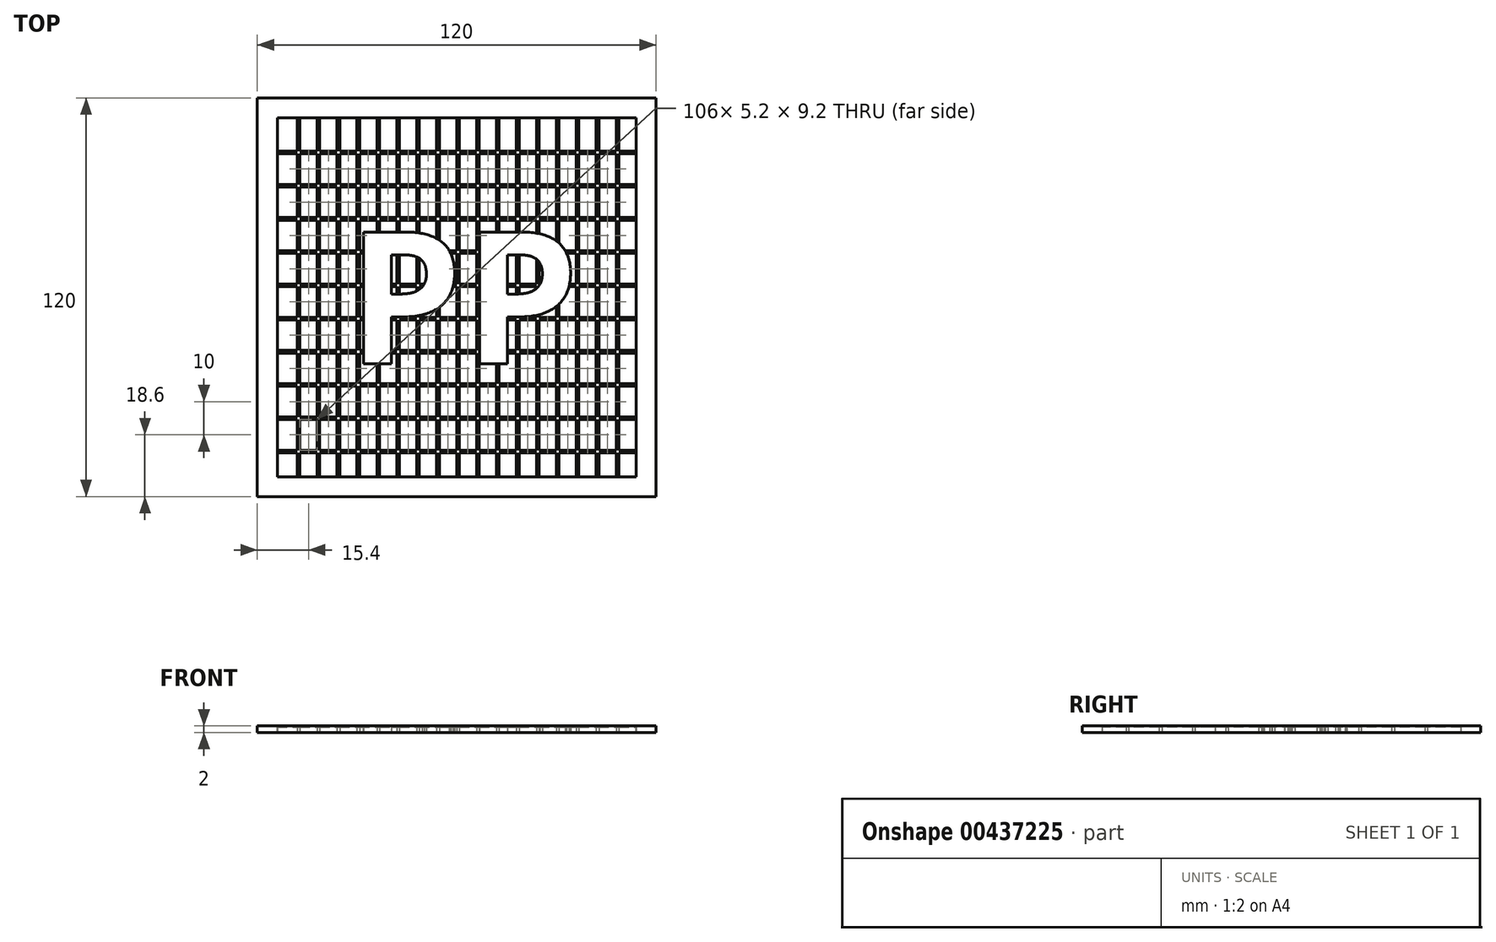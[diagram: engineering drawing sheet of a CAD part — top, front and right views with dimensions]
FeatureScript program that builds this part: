
annotation { "Feature Type Name" : "Feature", "Feature Type Description" : "" }
export const myFeature = defineFeature(function(context is Context, id is Id, definition is map)
    precondition{}
    {
        {
            var Q0;
            Q0=qCreatedBy(makeId("Top.planeOp"),FACE);
            var sketch = newSketch(context, id + "F0", { "sketchPlane" : qUnion([Q0])});
            skLineSegment(sketch, "E0.bottom", {"start": v(-61, 60) * mm, "end": v(59, 60) * mm});
            skLineSegment(sketch, "E0.top", {"start": v(-61, -60) * mm, "end": v(59, -60) * mm});
            skLineSegment(sketch, "E0.left", {"start": v(-61, 60) * mm, "end": v(-61, -60) * mm});
            skLineSegment(sketch, "E0.right", {"start": v(59, 60) * mm, "end": v(59, -60) * mm});
            skLineSegment(sketch, "E1.bottom", {"start": v(-55, 54) * mm, "end": v(53, 54) * mm});
            skLineSegment(sketch, "E1.top", {"start": v(-55, -54) * mm, "end": v(53, -54) * mm});
            skLineSegment(sketch, "E1.left", {"start": v(-55, 54) * mm, "end": v(-55, -54) * mm});
            skLineSegment(sketch, "E1.right", {"start": v(53, 54) * mm, "end": v(53, -54) * mm});
            skSolve(sketch);
        }
        {
            var Q0;
            Q0 = qSketchRegion(id + "F0", true);
            extrude(context, id + "F1", {"entities" : qUnion([Q0]), "depth" : 2 * mm});
        }
        {
            var Q0;
            Q0=qCreatedBy(makeId("Top.planeOp"),FACE);
            var sketch = newSketch(context, id + "F2", { "sketchPlane" : qUnion([Q0])});
            skLineSegment(sketch, "E2.bottom", {"start": v(-60, 44) * mm, "end": v(58, 44) * mm});
            skLineSegment(sketch, "E2.top", {"start": v(-60, 43.2) * mm, "end": v(58, 43.2) * mm});
            skLineSegment(sketch, "E2.left", {"start": v(-60, 44) * mm, "end": v(-60, 43.2) * mm});
            skLineSegment(sketch, "E2.right", {"start": v(58, 44) * mm, "end": v(58, 43.2) * mm});
            skLineSegment(sketch, "E3.1.0.0", {"start": v(-60, 33.2) * mm, "end": v(58, 33.2) * mm});
            skLineSegment(sketch, "E3.1.0.1", {"start": v(-60, 34) * mm, "end": v(58, 34) * mm});
            skLineSegment(sketch, "E3.1.0.2", {"start": v(-60, 34) * mm, "end": v(-60, 33.2) * mm});
            skLineSegment(sketch, "E3.1.0.3", {"start": v(58, 34) * mm, "end": v(58, 33.2) * mm});
            skLineSegment(sketch, "E3.2.0.0", {"start": v(-59.99, 23.2) * mm, "end": v(58.01, 23.2) * mm});
            skLineSegment(sketch, "E3.2.0.1", {"start": v(-59.99, 24) * mm, "end": v(58.01, 24) * mm});
            skLineSegment(sketch, "E3.2.0.2", {"start": v(-59.99, 24) * mm, "end": v(-59.99, 23.2) * mm});
            skLineSegment(sketch, "E3.2.0.3", {"start": v(58.01, 24) * mm, "end": v(58.01, 23.2) * mm});
            skLineSegment(sketch, "E3.3.0.0", {"start": v(-59.98, 13.2) * mm, "end": v(58.02, 13.2) * mm});
            skLineSegment(sketch, "E3.3.0.1", {"start": v(-59.98, 14) * mm, "end": v(58.02, 14) * mm});
            skLineSegment(sketch, "E3.3.0.2", {"start": v(-59.98, 14) * mm, "end": v(-59.98, 13.2) * mm});
            skLineSegment(sketch, "E3.3.0.3", {"start": v(58.02, 14) * mm, "end": v(58.02, 13.2) * mm});
            skLineSegment(sketch, "E3.4.0.0", {"start": v(-59.97, 3.2) * mm, "end": v(58.03, 3.2) * mm});
            skLineSegment(sketch, "E3.4.0.1", {"start": v(-59.97, 4) * mm, "end": v(58.03, 4) * mm});
            skLineSegment(sketch, "E3.4.0.2", {"start": v(-59.97, 4) * mm, "end": v(-59.97, 3.2) * mm});
            skLineSegment(sketch, "E3.4.0.3", {"start": v(58.03, 4) * mm, "end": v(58.03, 3.2) * mm});
            skLineSegment(sketch, "E3.5.0.0", {"start": v(-59.96, -6.8) * mm, "end": v(58.04, -6.8) * mm});
            skLineSegment(sketch, "E3.5.0.1", {"start": v(-59.96, -6) * mm, "end": v(58.04, -6) * mm});
            skLineSegment(sketch, "E3.5.0.2", {"start": v(-59.96, -6) * mm, "end": v(-59.96, -6.8) * mm});
            skLineSegment(sketch, "E3.5.0.3", {"start": v(58.04, -6) * mm, "end": v(58.04, -6.8) * mm});
            skLineSegment(sketch, "E3.6.0.0", {"start": v(-59.96, -16.8) * mm, "end": v(58.04, -16.8) * mm});
            skLineSegment(sketch, "E3.6.0.1", {"start": v(-59.96, -16) * mm, "end": v(58.04, -16) * mm});
            skLineSegment(sketch, "E3.6.0.2", {"start": v(-59.96, -16) * mm, "end": v(-59.96, -16.8) * mm});
            skLineSegment(sketch, "E3.6.0.3", {"start": v(58.04, -16) * mm, "end": v(58.04, -16.8) * mm});
            skLineSegment(sketch, "E3.7.0.0", {"start": v(-59.95, -26.8) * mm, "end": v(58.05, -26.8) * mm});
            skLineSegment(sketch, "E3.7.0.1", {"start": v(-59.95, -26) * mm, "end": v(58.05, -26) * mm});
            skLineSegment(sketch, "E3.7.0.2", {"start": v(-59.95, -26) * mm, "end": v(-59.95, -26.8) * mm});
            skLineSegment(sketch, "E3.7.0.3", {"start": v(58.05, -26) * mm, "end": v(58.05, -26.8) * mm});
            skLineSegment(sketch, "E3.8.0.0", {"start": v(-59.94, -36.8) * mm, "end": v(58.06, -36.8) * mm});
            skLineSegment(sketch, "E3.8.0.1", {"start": v(-59.94, -36) * mm, "end": v(58.06, -36) * mm});
            skLineSegment(sketch, "E3.8.0.2", {"start": v(-59.94, -36) * mm, "end": v(-59.94, -36.8) * mm});
            skLineSegment(sketch, "E3.8.0.3", {"start": v(58.06, -36) * mm, "end": v(58.06, -36.8) * mm});
            skLineSegment(sketch, "E3.9.0.0", {"start": v(-59.93, -46.8) * mm, "end": v(58.07, -46.8) * mm});
            skLineSegment(sketch, "E3.9.0.1", {"start": v(-59.93, -46) * mm, "end": v(58.07, -46) * mm});
            skLineSegment(sketch, "E3.9.0.2", {"start": v(-59.93, -46) * mm, "end": v(-59.93, -46.8) * mm});
            skLineSegment(sketch, "E3.9.0.3", {"start": v(58.07, -46) * mm, "end": v(58.07, -46.8) * mm});
            skLineSegment(sketch, "E3.direction1", {"start": v(-60, 43.2) * mm, "end": v(-60, 33.2) * mm, "construction": true});
            skSolve(sketch);
        }
        {
            var Q0;
            Q0 = qSketchRegion(id + "F2", true);
            extrude(context, id + "F3", {"entities" : qUnion([Q0]), "operationType" : NewBodyOperationType.ADD, "depth" : 1.6 * mm});
        }
        {
            var Q0;
            Q0=qCreatedBy(makeId("Top.planeOp"),FACE);
            var sketch = newSketch(context, id + "F4", { "sketchPlane" : qUnion([Q0])});
            skLineSegment(sketch, "E4.bottom", {"start": v(-49, 57.34) * mm, "end": v(-48.2, 57.34) * mm});
            skLineSegment(sketch, "E4.top", {"start": v(-49, -57.66) * mm, "end": v(-48.2, -57.66) * mm});
            skLineSegment(sketch, "E4.left", {"start": v(-49, 57.34) * mm, "end": v(-49, -57.66) * mm});
            skLineSegment(sketch, "E4.right", {"start": v(-48.2, 57.34) * mm, "end": v(-48.2, -57.66) * mm});
            skLineSegment(sketch, "E5.1.0.0", {"start": v(-42.2, 57.34) * mm, "end": v(-42.2, -57.66) * mm});
            skLineSegment(sketch, "E5.1.0.1", {"start": v(-43, 57.34) * mm, "end": v(-43, -57.66) * mm});
            skLineSegment(sketch, "E5.1.0.2", {"start": v(-43, -57.66) * mm, "end": v(-42.2, -57.66) * mm});
            skLineSegment(sketch, "E5.1.0.3", {"start": v(-43, 57.34) * mm, "end": v(-42.2, 57.34) * mm});
            skLineSegment(sketch, "E5.2.0.0", {"start": v(-36.2, 57.34) * mm, "end": v(-36.2, -57.66) * mm});
            skLineSegment(sketch, "E5.2.0.1", {"start": v(-37, 57.34) * mm, "end": v(-37, -57.66) * mm});
            skLineSegment(sketch, "E5.2.0.2", {"start": v(-37, -57.66) * mm, "end": v(-36.2, -57.66) * mm});
            skLineSegment(sketch, "E5.2.0.3", {"start": v(-37, 57.34) * mm, "end": v(-36.2, 57.34) * mm});
            skLineSegment(sketch, "E5.3.0.0", {"start": v(-30.2, 57.34) * mm, "end": v(-30.2, -57.66) * mm});
            skLineSegment(sketch, "E5.3.0.1", {"start": v(-31, 57.34) * mm, "end": v(-31, -57.66) * mm});
            skLineSegment(sketch, "E5.3.0.2", {"start": v(-31, -57.66) * mm, "end": v(-30.2, -57.66) * mm});
            skLineSegment(sketch, "E5.3.0.3", {"start": v(-31, 57.34) * mm, "end": v(-30.2, 57.34) * mm});
            skLineSegment(sketch, "E5.4.0.0", {"start": v(-24.2, 57.34) * mm, "end": v(-24.2, -57.66) * mm});
            skLineSegment(sketch, "E5.4.0.1", {"start": v(-25, 57.34) * mm, "end": v(-25, -57.66) * mm});
            skLineSegment(sketch, "E5.4.0.2", {"start": v(-25, -57.66) * mm, "end": v(-24.2, -57.66) * mm});
            skLineSegment(sketch, "E5.4.0.3", {"start": v(-25, 57.34) * mm, "end": v(-24.2, 57.34) * mm});
            skLineSegment(sketch, "E5.5.0.0", {"start": v(-18.2, 57.34) * mm, "end": v(-18.2, -57.66) * mm});
            skLineSegment(sketch, "E5.5.0.1", {"start": v(-19, 57.34) * mm, "end": v(-19, -57.66) * mm});
            skLineSegment(sketch, "E5.5.0.2", {"start": v(-19, -57.66) * mm, "end": v(-18.2, -57.66) * mm});
            skLineSegment(sketch, "E5.5.0.3", {"start": v(-19, 57.34) * mm, "end": v(-18.2, 57.34) * mm});
            skLineSegment(sketch, "E5.6.0.0", {"start": v(-12.2, 57.34) * mm, "end": v(-12.2, -57.66) * mm});
            skLineSegment(sketch, "E5.6.0.1", {"start": v(-13, 57.34) * mm, "end": v(-13, -57.66) * mm});
            skLineSegment(sketch, "E5.6.0.2", {"start": v(-13, -57.66) * mm, "end": v(-12.2, -57.66) * mm});
            skLineSegment(sketch, "E5.6.0.3", {"start": v(-13, 57.34) * mm, "end": v(-12.2, 57.34) * mm});
            skLineSegment(sketch, "E5.7.0.0", {"start": v(-6.2, 57.34) * mm, "end": v(-6.2, -57.66) * mm});
            skLineSegment(sketch, "E5.7.0.1", {"start": v(-7, 57.34) * mm, "end": v(-7, -57.66) * mm});
            skLineSegment(sketch, "E5.7.0.2", {"start": v(-7, -57.66) * mm, "end": v(-6.2, -57.66) * mm});
            skLineSegment(sketch, "E5.7.0.3", {"start": v(-7, 57.34) * mm, "end": v(-6.2, 57.34) * mm});
            skLineSegment(sketch, "E5.8.0.0", {"start": v(-0.2, 57.34) * mm, "end": v(-0.2, -57.66) * mm});
            skLineSegment(sketch, "E5.8.0.1", {"start": v(-1, 57.34) * mm, "end": v(-1, -57.66) * mm});
            skLineSegment(sketch, "E5.8.0.2", {"start": v(-1, -57.66) * mm, "end": v(-0.2, -57.66) * mm});
            skLineSegment(sketch, "E5.8.0.3", {"start": v(-1, 57.34) * mm, "end": v(-0.2, 57.34) * mm});
            skLineSegment(sketch, "E5.9.0.0", {"start": v(5.8, 57.34) * mm, "end": v(5.8, -57.66) * mm});
            skLineSegment(sketch, "E5.9.0.1", {"start": v(5, 57.34) * mm, "end": v(5, -57.66) * mm});
            skLineSegment(sketch, "E5.9.0.2", {"start": v(5, -57.66) * mm, "end": v(5.8, -57.66) * mm});
            skLineSegment(sketch, "E5.9.0.3", {"start": v(5, 57.34) * mm, "end": v(5.8, 57.34) * mm});
            skLineSegment(sketch, "E5.10.0.0", {"start": v(11.8, 57.34) * mm, "end": v(11.8, -57.66) * mm});
            skLineSegment(sketch, "E5.10.0.1", {"start": v(11, 57.34) * mm, "end": v(11, -57.66) * mm});
            skLineSegment(sketch, "E5.10.0.2", {"start": v(11, -57.66) * mm, "end": v(11.8, -57.66) * mm});
            skLineSegment(sketch, "E5.10.0.3", {"start": v(11, 57.34) * mm, "end": v(11.8, 57.34) * mm});
            skLineSegment(sketch, "E5.11.0.0", {"start": v(17.8, 57.34) * mm, "end": v(17.8, -57.66) * mm});
            skLineSegment(sketch, "E5.11.0.1", {"start": v(17, 57.34) * mm, "end": v(17, -57.66) * mm});
            skLineSegment(sketch, "E5.11.0.2", {"start": v(17, -57.66) * mm, "end": v(17.8, -57.66) * mm});
            skLineSegment(sketch, "E5.11.0.3", {"start": v(17, 57.34) * mm, "end": v(17.8, 57.34) * mm});
            skLineSegment(sketch, "E5.12.0.0", {"start": v(23.8, 57.34) * mm, "end": v(23.8, -57.66) * mm});
            skLineSegment(sketch, "E5.12.0.1", {"start": v(23, 57.34) * mm, "end": v(23, -57.66) * mm});
            skLineSegment(sketch, "E5.12.0.2", {"start": v(23, -57.66) * mm, "end": v(23.8, -57.66) * mm});
            skLineSegment(sketch, "E5.12.0.3", {"start": v(23, 57.34) * mm, "end": v(23.8, 57.34) * mm});
            skLineSegment(sketch, "E5.13.0.0", {"start": v(29.8, 57.34) * mm, "end": v(29.8, -57.66) * mm});
            skLineSegment(sketch, "E5.13.0.1", {"start": v(29, 57.34) * mm, "end": v(29, -57.66) * mm});
            skLineSegment(sketch, "E5.13.0.2", {"start": v(29, -57.66) * mm, "end": v(29.8, -57.66) * mm});
            skLineSegment(sketch, "E5.13.0.3", {"start": v(29, 57.34) * mm, "end": v(29.8, 57.34) * mm});
            skLineSegment(sketch, "E5.14.0.0", {"start": v(35.8, 57.34) * mm, "end": v(35.8, -57.66) * mm});
            skLineSegment(sketch, "E5.14.0.1", {"start": v(35, 57.34) * mm, "end": v(35, -57.66) * mm});
            skLineSegment(sketch, "E5.14.0.2", {"start": v(35, -57.66) * mm, "end": v(35.8, -57.66) * mm});
            skLineSegment(sketch, "E5.14.0.3", {"start": v(35, 57.34) * mm, "end": v(35.8, 57.34) * mm});
            skLineSegment(sketch, "E5.15.0.0", {"start": v(41.8, 57.34) * mm, "end": v(41.8, -57.66) * mm});
            skLineSegment(sketch, "E5.15.0.1", {"start": v(41, 57.34) * mm, "end": v(41, -57.66) * mm});
            skLineSegment(sketch, "E5.15.0.2", {"start": v(41, -57.66) * mm, "end": v(41.8, -57.66) * mm});
            skLineSegment(sketch, "E5.15.0.3", {"start": v(41, 57.34) * mm, "end": v(41.8, 57.34) * mm});
            skLineSegment(sketch, "E5.16.0.0", {"start": v(47.8, 57.34) * mm, "end": v(47.8, -57.66) * mm});
            skLineSegment(sketch, "E5.16.0.1", {"start": v(47, 57.34) * mm, "end": v(47, -57.66) * mm});
            skLineSegment(sketch, "E5.16.0.2", {"start": v(47, -57.66) * mm, "end": v(47.8, -57.66) * mm});
            skLineSegment(sketch, "E5.16.0.3", {"start": v(47, 57.34) * mm, "end": v(47.8, 57.34) * mm});
            skLineSegment(sketch, "E5.direction1", {"start": v(-49, -57.66) * mm, "end": v(-43, -57.66) * mm, "construction": true});
            skSolve(sketch);
        }
        {
            var Q0;
            Q0 = qSketchRegion(id + "F4", true);
            extrude(context, id + "F5", {"entities" : qUnion([Q0]), "operationType" : NewBodyOperationType.ADD, "depth" : 1.6 * mm});
        }
        {
            var Q0;
            Q0=qCreatedBy(makeId("Top.planeOp"),FACE);
            var sketch = newSketch(context, id + "F6", { "sketchPlane" : qUnion([Q0])});
            skText(sketch, "E6", { "text": "PP\n", "fontName": "OpenSans-Bold.ttf"});
            const initialGuessF6  = {"E6": [-0.034, -0.02, 1, 0, 0.04]};
            skSetInitialGuess(sketch, initialGuessF6);
            skSolve(sketch);
        }
        {
            var Q0;
            Q0 = qSketchRegion(id + "F6", true);
            extrude(context, id + "F7", {"entities" : qUnion([Q0]), "operationType" : NewBodyOperationType.ADD, "depth" : 2 * mm});
        }
    });
